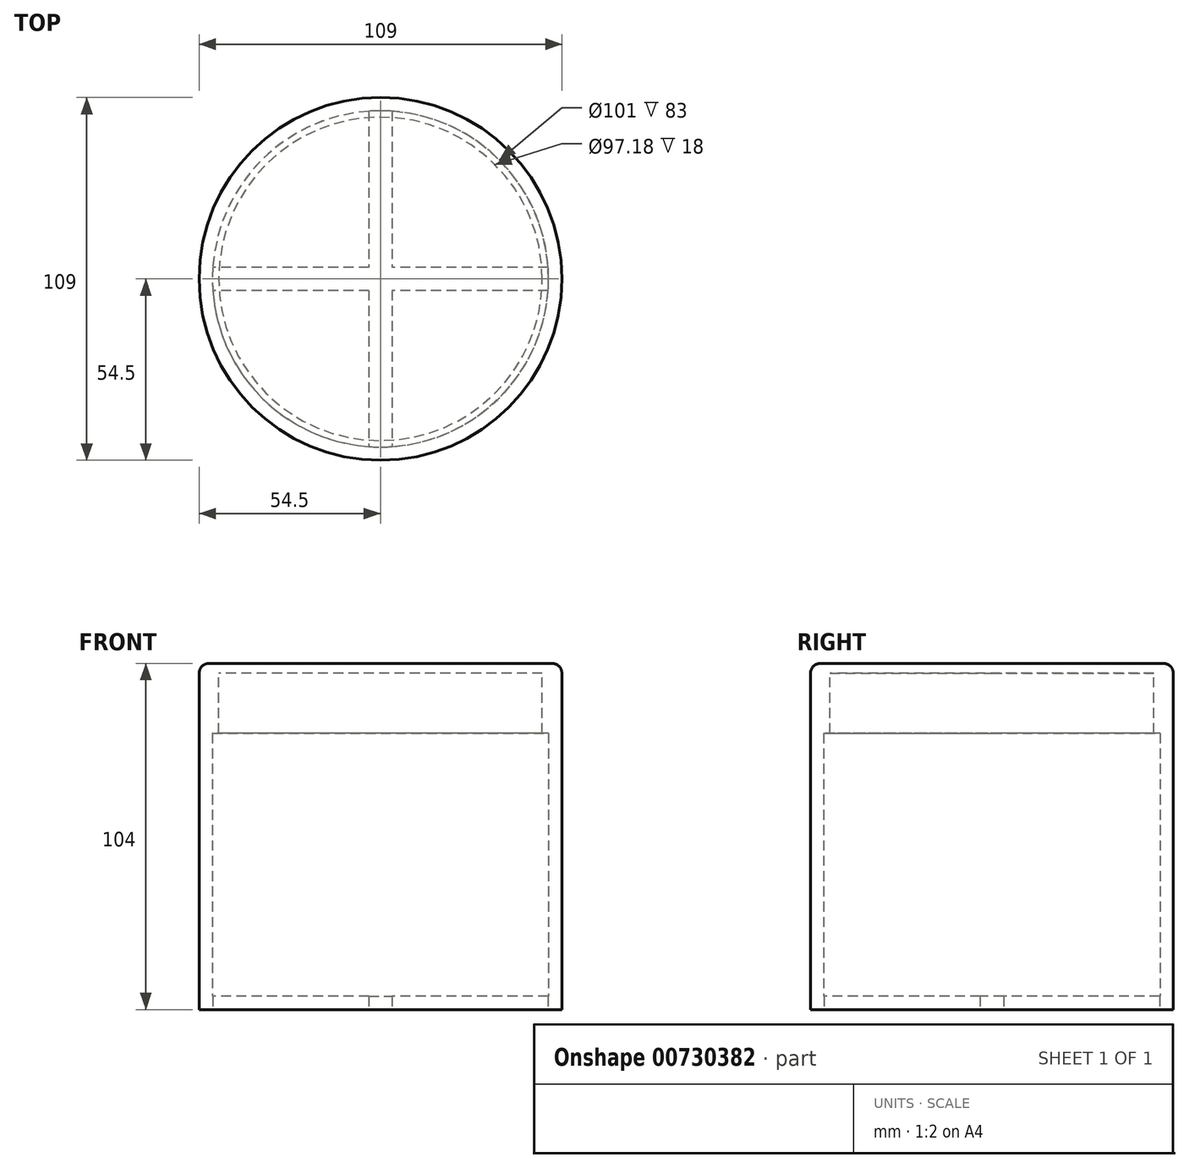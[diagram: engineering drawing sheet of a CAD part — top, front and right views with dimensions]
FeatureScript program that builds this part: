
annotation { "Feature Type Name" : "Feature", "Feature Type Description" : "" }
export const myFeature = defineFeature(function(context is Context, id is Id, definition is map)
    precondition{}
    {
        {
            var Q0;
            Q0=qCreatedBy(makeId("Top.planeOp"),FACE);
            var sketch = newSketch(context, id + "F0", { "sketchPlane" : qUnion([Q0])});
            skCircle(sketch, "E0", {"center": v(0, 0) * mm, "radius": 50.5 * mm});
            skCircle(sketch, "E1", {"center": v(0, 0) * mm, "radius": 54.5 * mm});
            skLineSegment(sketch, "E2.left", {"start": v(-3.5, 50.38) * mm, "end": v(-3.5, -50.38) * mm});
            skLineSegment(sketch, "E2.right", {"start": v(3.5, 50.38) * mm, "end": v(3.5, -50.38) * mm});
            skLineSegment(sketch, "E3.bottom", {"start": v(50.38, 3.5) * mm, "end": v(-50.38, 3.5) * mm});
            skLineSegment(sketch, "E3.top", {"start": v(50.38, -3.5) * mm, "end": v(-50.38, -3.5) * mm});
            skPoint(sketch, "E2.bottom.end.orphan", {"position": v(3.5, 52.04) * mm});
            skPoint(sketch, "E2.bottom.start.orphan", {"position": v(-3.5, 52.04) * mm});
            skPoint(sketch, "E3.right.start.orphan", {"position": v(-52.04, 3.5) * mm});
            skPoint(sketch, "E4.orphan", {"position": v(-52.04, -3.5) * mm});
            skPoint(sketch, "E5.orphan", {"position": v(52.04, 3.5) * mm});
            skPoint(sketch, "E6.orphan", {"position": v(52.04, -3.5) * mm});
            skPoint(sketch, "E7.orphan", {"position": v(3.5, -52.04) * mm});
            skPoint(sketch, "E8.orphan", {"position": v(-3.5, -52.04) * mm});
            skSolve(sketch);
        }
        {
            var Q0;
            Q0=makeQuery(id+"F0.imprint","IMPRINT",FACE,{"disambiguationData":[TD([[makeQuery(id+"F0.imprint","IMPRINT",EDGE,{"derivedFrom":sQuery(id+"F0.wireOp",EDGE,"E1")}),1.0]])]});
            extrude(context, id + "F1", {"entities" : qUnion([Q0]), "depth" : 90 * mm, "offsetDistance" : 25 * mm});
        }
        {
            var Q0;
            {var subQ0=sQuery(id+"F0.wireOp",EDGE,"E3.bottom");var subQ1=sQuery(id+"F0.wireOp",EDGE,"E2.left");var subQ2=makeQuery(id+"F0.imprint","INTERSECT",VERTEX,{"derivedFrom":[subQ1,subQ0]});Q0=makeQuery(id+"F0.imprint","IMPRINT",FACE,{"disambiguationData":[TD([[makeQuery(id+"F0.imprint","IMPRINT",EDGE,{"disambiguationData":[TD([[subQ2,-1.0]])],"derivedFrom":subQ1}),1.0]])]});}
            var Q1;
            {var subQ0=sQuery(id+"F0.wireOp",EDGE,"E2.left");var subQ1=sQuery(id+"F0.wireOp",EDGE,"E0");var subQ2=makeQuery(id+"F0.imprint","INTERSECT",VERTEX,{"disambiguationData":[OD(1.0)],"derivedFrom":[subQ1,subQ0]});Q1=makeQuery(id+"F0.imprint","IMPRINT",FACE,{"disambiguationData":[TD([[makeQuery(id+"F0.imprint","IMPRINT",EDGE,{"disambiguationData":[TD([[subQ2,-1.0]])],"derivedFrom":subQ1}),1.0]])]});}
            var Q2;
            {var subQ0=sQuery(id+"F0.wireOp",EDGE,"E3.bottom");var subQ1=sQuery(id+"F0.wireOp",EDGE,"E0");var subQ2=makeQuery(id+"F0.imprint","INTERSECT",VERTEX,{"disambiguationData":[OD(0.0)],"derivedFrom":[subQ1,subQ0]});Q2=makeQuery(id+"F0.imprint","IMPRINT",FACE,{"disambiguationData":[TD([[makeQuery(id+"F0.imprint","IMPRINT",EDGE,{"disambiguationData":[TD([[subQ2,1.0]])],"derivedFrom":subQ1}),1.0]])]});}
            var Q3;
            {var subQ0=sQuery(id+"F0.wireOp",EDGE,"E2.left");var subQ1=sQuery(id+"F0.wireOp",EDGE,"E0");var subQ2=makeQuery(id+"F0.imprint","INTERSECT",VERTEX,{"disambiguationData":[OD(0.0)],"derivedFrom":[subQ1,subQ0]});Q3=makeQuery(id+"F0.imprint","IMPRINT",FACE,{"disambiguationData":[TD([[makeQuery(id+"F0.imprint","IMPRINT",EDGE,{"disambiguationData":[TD([[subQ2,1.0]])],"derivedFrom":subQ1}),1.0]])]});}
            var Q4;
            {var subQ0=sQuery(id+"F0.wireOp",EDGE,"E3.bottom");var subQ1=sQuery(id+"F0.wireOp",EDGE,"E0");var subQ2=makeQuery(id+"F0.imprint","INTERSECT",VERTEX,{"disambiguationData":[OD(1.0)],"derivedFrom":[subQ1,subQ0]});Q4=makeQuery(id+"F0.imprint","IMPRINT",FACE,{"disambiguationData":[TD([[makeQuery(id+"F0.imprint","IMPRINT",EDGE,{"disambiguationData":[TD([[subQ2,-1.0]])],"derivedFrom":subQ1}),1.0]])]});}
            extrude(context, id + "F2", {"entities" : qUnion([Q0, Q1, Q2, Q3, Q4]), "operationType" : NewBodyOperationType.ADD, "depth" : 4 * mm, "offsetDistance" : 25 * mm});
        }
        {
            var Q0;
            Q0=makeQuery(id+"F1.opExtrude","CAP_FACE",FACE,{"disambiguationData":[OSD([sQuery(id+"F0.wireOp",EDGE,"E0"),sQuery(id+"F0.wireOp",EDGE,"E1")])],"isStart":false});
            var sketch = newSketch(context, id + "F3", { "sketchPlane" : qUnion([Q0])});
            skCircle(sketch, "E9", {"center": v(0, 0) * mm, "radius": 51.5 * mm});
            skCircle(sketch, "E10", {"center": v(0, 0) * mm, "radius": 54.5 * mm});
            skSolve(sketch);
        }
        {
            var Q0;
            Q0=makeQuery(id+"F3.imprint","IMPRINT",FACE,{"disambiguationData":[TD([[makeQuery(id+"F3.imprint","IMPRINT",EDGE,{"derivedFrom":sQuery(id+"F3.wireOp",EDGE,"E9")}),-1.0]])]});
            extrude(context, id + "F4", {"entities" : qUnion([Q0]), "depth" : 11 * mm, "offsetDistance" : 25 * mm});
        }
        {
            var Q0;
            Q0=makeQuery(id+"F4.opExtrude","CAP_FACE",FACE,{"disambiguationData":[OSD([sQuery(id+"F3.wireOp",EDGE,"E9"),sQuery(id+"F3.wireOp",EDGE,"E10")])],"isStart":false});
            var sketch = newSketch(context, id + "F5", { "sketchPlane" : qUnion([Q0])});
            skCircle(sketch, "E11", {"center": v(0, 0) * mm, "radius": 54.5 * mm});
            skCircle(sketch, "E12", {"center": v(0, 0) * mm, "radius": 48.6 * mm});
            skCircle(sketch, "E13", {"center": v(0, 0) * mm, "radius": 51.5 * mm});
            skSolve(sketch);
        }
        {
            var Q0;
            Q0 = qSketchRegion(id + "F5", true);
            var Q1;
            Q1=makeQuery(id+"F5.imprint","IMPRINT",FACE,{"disambiguationData":[TD([[makeQuery(id+"F5.imprint","IMPRINT",EDGE,{"derivedFrom":sQuery(id+"F5.wireOp",EDGE,"E12")}),1.0]])]});
            var Q2;
            Q2=makeQuery(id+"F5.imprint","IMPRINT",FACE,{"disambiguationData":[TD([[makeQuery(id+"F5.imprint","IMPRINT",EDGE,{"derivedFrom":sQuery(id+"F5.wireOp",EDGE,"E12")}),-1.0]])]});
            extrude(context, id + "F6", {"entities" : qUnion([Q0, Q1, Q2]), "operationType" : NewBodyOperationType.ADD, "depth" : 3 * mm, "offsetDistance" : 25 * mm});
        }
        {
            var Q0;
            Q0=makeQuery(id+"F6.opExtrude","CAP_EDGE",EDGE,{"disambiguationData":[OSD([sQuery(id+"F5.wireOp",EDGE,"E11")])],"isStart":false});
            fillet(context, id + "F7", {"entities" : qUnion([Q0]), "radius" : 3 * mm, "tangentPropagation" : true, "allowEdgeOverflow" : false});
        }
        {
            var Q0;
            Q0=makeQuery(id+"F5.imprint","IMPRINT",FACE,{"disambiguationData":[TD([[makeQuery(id+"F5.imprint","IMPRINT",EDGE,{"derivedFrom":sQuery(id+"F5.wireOp",EDGE,"E12")}),-1.0]])]});
            extrude(context, id + "F8", {"entities" : qUnion([Q0]), "operationType" : NewBodyOperationType.ADD, "oppositeDirection" : true, "depth" : 18 * mm, "offsetDistance" : 25 * mm});
        }
    });
